# Revit family: QF_BOURGEAT_CARAVANE_Meubles_buffet_cuve_froid_statique_baie_libre_simple_accès
name_source: partatom
category: Equipement spécialisé
revit_build: Autodesk Revit 2015 (Build: 20140606_1530(x64)
units: mm (PartAtom-declared; Revit-internal decimal feet)

## types (2) — shared parameters
Charge max = 100.00 kg
Charge maximale = 100 kg
Fabricant = BOURGEAT
Fréquence = 50 Hz
Hauteur hors tout = 1385 mm
Hauteur plan de travail = 839 mm  [stored 2.75262 ft]
Indice de protection = 21
Inox = Acier inoxydable, poli
Intensité nominale = 1 A
Phase = 2
Profondeur hors tout = 840 mm
Puissance électrique  = 300 W
Spécification du Fabricant = Meuble buffet cuve Froid statique -baie libre
Tension = 230 V
Type Fluide Frigorigène = R404a
URL catalogue = http://www.bourgeat.fr

## per-type parameters (varying)
| type | Longueur de la tablette | Longueur hors tout | Longueur pare-haleine | Modèle | Poids net à vide | Poids à vide | Puissance frigorifique |
| Modèle simple accès 3 GN | 1055 mm | 1315 mm | 1080 mm | 856013 | 200.00 kg | 200 kg | 272 W à -5° |
| Modèle simple accès 4 GN | 1380 mm  [stored 4.52756 ft] | 1640 mm  [stored 5.38058 ft] | 1405 mm  [stored 4.60958 ft] | 856014 | 220.00 kg | 220 | 272W à -5°C |

note: [stored X ft] marks values corroborated as IEEE doubles in the binary element streams (Revit-internal decimal feet)

## geometry (parser evidence)
native form markers: Blend x4
no freeform markers — native parametric forms only
